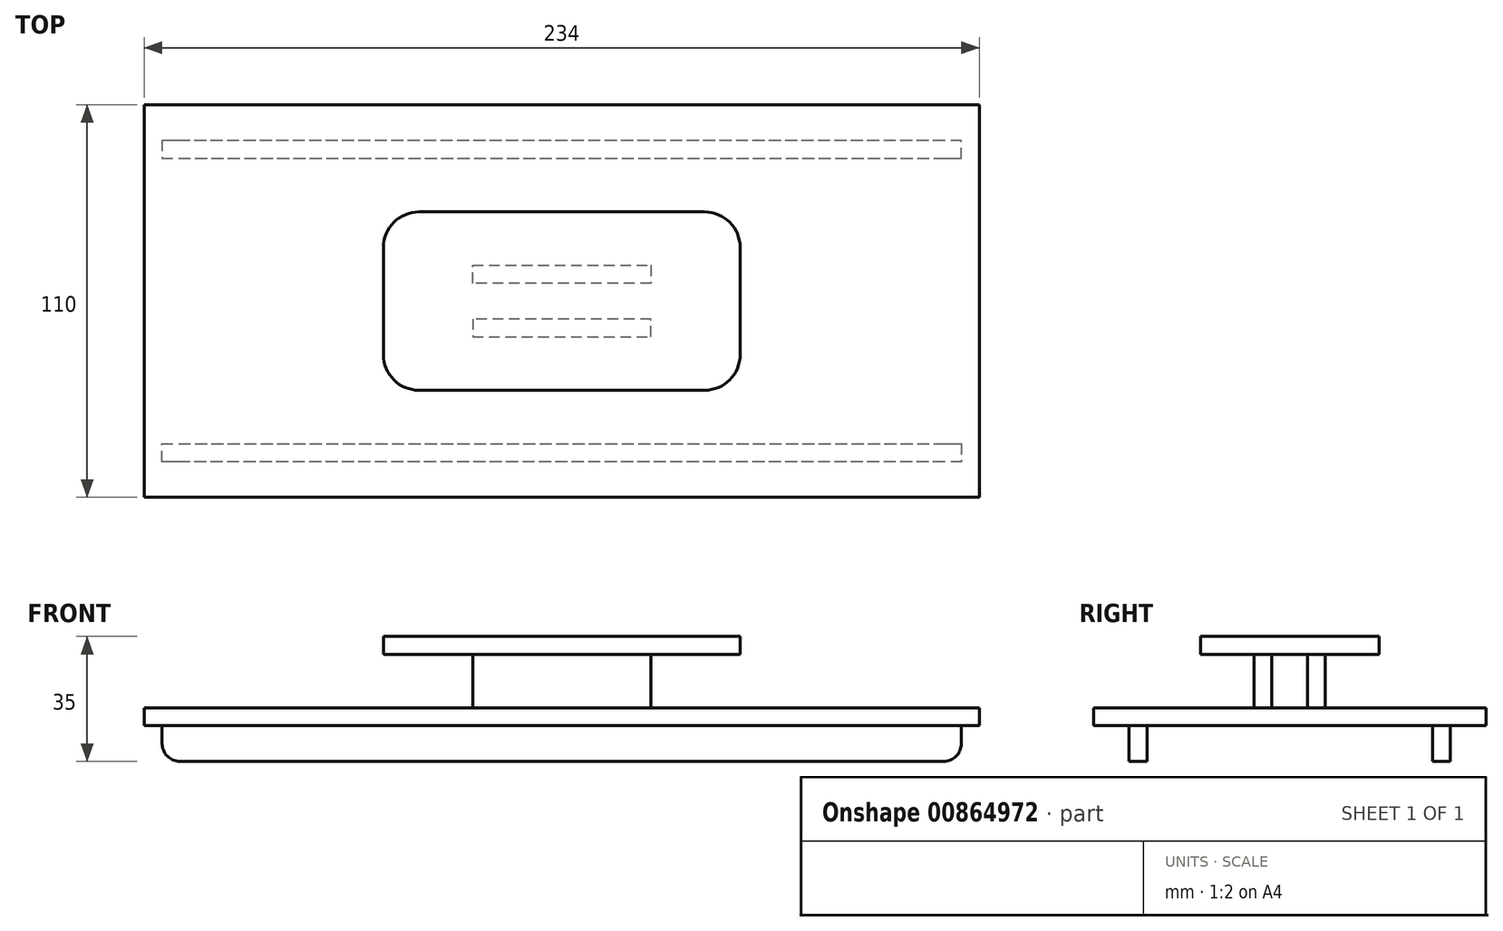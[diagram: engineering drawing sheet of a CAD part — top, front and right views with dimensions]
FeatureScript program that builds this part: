
annotation { "Feature Type Name" : "Feature", "Feature Type Description" : "" }
export const myFeature = defineFeature(function(context is Context, id is Id, definition is map)
    precondition{}
    {
        {
            var Q0;
            Q0=qCreatedBy(makeId("Top.planeOp"),FACE);
            var sketch = newSketch(context, id + "F0", { "sketchPlane" : qUnion([Q0])});
            skLineSegment(sketch, "E0", {"start": v(0, 55) * mm, "end": v(-117, 55) * mm});
            skLineSegment(sketch, "E1", {"start": v(-117, 55) * mm, "end": v(-117, -55) * mm});
            skLineSegment(sketch, "E2", {"start": v(-117, -55) * mm, "end": v(117, -55) * mm});
            skLineSegment(sketch, "E3", {"start": v(117, -55) * mm, "end": v(117, 55) * mm});
            skLineSegment(sketch, "E4", {"start": v(117, 55) * mm, "end": v(0, 55) * mm});
            skSolve(sketch);
        }
        {
            var Q0;
            Q0=makeQuery(id+"F0.imprint","IMPRINT",FACE,{"disambiguationData":[TD([[makeQuery(id+"F0.imprint","IMPRINT",EDGE,{"derivedFrom":sQuery(id+"F0.wireOp",EDGE,"LMLZs7OO-DFld-XzK2-CuK9-4s45sYu2oxnE")}),1.0]])]});
            var Q1;
            Q1=makeQuery(id+"F0.imprint","IMPRINT",FACE,{"disambiguationData":[TD([[makeQuery(id+"F0.imprint","IMPRINT",EDGE,{"derivedFrom":sQuery(id+"F0.wireOp",EDGE,"cvSQRNAl-XPxT-cCQd-Kg4y-DsinOLvF7RYH")}),1.0]])]});
            var Q2;
            Q2=makeQuery(id+"F0.imprint","IMPRINT",FACE,{"disambiguationData":[TD([[makeQuery(id+"F0.imprint","IMPRINT",EDGE,{"derivedFrom":sQuery(id+"F0.wireOp",EDGE,"E0")}),1.0]])]});
            extrude(context, id + "F1", {"entities" : qUnion([Q0, Q1, Q2]), "depth" : 5 * mm, "offsetDistance" : 25 * mm});
        }
        {
            var Q0;
            Q0=qCreatedBy(makeId("Top.planeOp"),FACE);
            var sketch = newSketch(context, id + "F2", { "sketchPlane" : qUnion([Q0])});
            skLineSegment(sketch, "E5", {"start": v(0, 45) * mm, "end": v(-112, 45) * mm});
            skLineSegment(sketch, "E6", {"start": v(-112, 45) * mm, "end": v(-112, 40) * mm});
            skLineSegment(sketch, "E7", {"start": v(-112, 40) * mm, "end": v(112, 40) * mm});
            skLineSegment(sketch, "E8", {"start": v(112, 40) * mm, "end": v(112, 45) * mm});
            skLineSegment(sketch, "E9", {"start": v(112, 45) * mm, "end": v(0, 45) * mm});
            skLineSegment(sketch, "E10.MirrorCS", {"start": v(-112, -45) * mm, "end": v(-112, -40) * mm});
            skLineSegment(sketch, "E11.MirrorCS", {"start": v(112, -40) * mm, "end": v(112, -45) * mm});
            skLineSegment(sketch, "E12.MirrorCS", {"start": v(0, -45) * mm, "end": v(-112, -45) * mm});
            skLineSegment(sketch, "E13.MirrorCS", {"start": v(-112, -40) * mm, "end": v(112, -40) * mm});
            skLineSegment(sketch, "E14.MirrorCS", {"start": v(112, -45) * mm, "end": v(0, -45) * mm});
            skSolve(sketch);
        }
        {
            var Q0;
            Q0=qCreatedBy(makeId("Top.planeOp"),FACE);
            cPlane(context, id + "F3", {"entities" : qUnion([Q0]), "cplaneType" : CPlaneType.OFFSET, "offset" : 25 * mm, "width" : 150 * mm, "height" : 150 * mm});
        }
        {
            var Q0;
            Q0=qCreatedBy(id+"F3.planeOp",FACE);
            var sketch = newSketch(context, id + "F4", { "sketchPlane" : qUnion([Q0])});
            skLineSegment(sketch, "E15", {"start": v(0, 25) * mm, "end": v(-40, 25) * mm});
            skLineSegment(sketch, "E16", {"start": v(-50, 15) * mm, "end": v(-50, -15) * mm});
            skLineSegment(sketch, "E17", {"start": v(-40, -25) * mm, "end": v(40, -25) * mm});
            skLineSegment(sketch, "E18", {"start": v(50, -15) * mm, "end": v(50, 15) * mm});
            skLineSegment(sketch, "E19", {"start": v(40, 25) * mm, "end": v(0, 25) * mm});
            skPoint(sketch, "E20.visualSharp", {"position": v(-50, 25) * mm});
            skArc(sketch, "E20.filletArc", {"start": v(-40, 25) * mm, "mid": v(-47.07, 22.07) * mm, "end": v(-50, 15) * mm});
            skPoint(sketch, "E21.visualSharp", {"position": v(50, 25) * mm});
            skArc(sketch, "E21.filletArc", {"start": v(50, 15) * mm, "mid": v(47.07, 22.07) * mm, "end": v(40, 25) * mm});
            skPoint(sketch, "E22.visualSharp", {"position": v(50, -25) * mm});
            skArc(sketch, "E22.filletArc", {"start": v(40, -25) * mm, "mid": v(47.07, -22.07) * mm, "end": v(50, -15) * mm});
            skPoint(sketch, "E23.visualSharp", {"position": v(-50, -25) * mm});
            skArc(sketch, "E23.filletArc", {"start": v(-50, -15) * mm, "mid": v(-47.07, -22.07) * mm, "end": v(-40, -25) * mm});
            skSolve(sketch);
        }
        {
            var Q0;
            Q0=qCreatedBy(makeId("Top.planeOp"),FACE);
            cPlane(context, id + "F5", {"entities" : qUnion([Q0]), "cplaneType" : CPlaneType.OFFSET, "offset" : 5 * mm, "width" : 150 * mm, "height" : 150 * mm});
        }
        {
            var Q0;
            Q0=qCreatedBy(id+"F5.planeOp",FACE);
            var sketch = newSketch(context, id + "F6", { "sketchPlane" : qUnion([Q0])});
            skLineSegment(sketch, "E24", {"start": v(0, 5) * mm, "end": v(-25, 5) * mm});
            skLineSegment(sketch, "E25", {"start": v(-25, 5) * mm, "end": v(-25, 10) * mm});
            skLineSegment(sketch, "E26", {"start": v(-25, 10) * mm, "end": v(25, 10) * mm});
            skLineSegment(sketch, "E27", {"start": v(25, 10) * mm, "end": v(25, 5) * mm});
            skLineSegment(sketch, "E28", {"start": v(25, 5) * mm, "end": v(0, 5) * mm});
            skLineSegment(sketch, "E29.MirrorCS", {"start": v(25, -5) * mm, "end": v(0, -5) * mm});
            skLineSegment(sketch, "E30.MirrorCS", {"start": v(-25, -10) * mm, "end": v(25, -10) * mm});
            skLineSegment(sketch, "E31.MirrorCS", {"start": v(25, -10) * mm, "end": v(25, -5) * mm});
            skLineSegment(sketch, "E32.MirrorCS", {"start": v(0, -5) * mm, "end": v(-25, -5) * mm});
            skLineSegment(sketch, "E33.MirrorCS", {"start": v(-25, -5) * mm, "end": v(-25, -10) * mm});
            skSolve(sketch);
        }
        {
            var Q0;
            Q0=makeQuery(id+"F2.imprint","IMPRINT",FACE,{"disambiguationData":[TD([[makeQuery(id+"F2.imprint","IMPRINT",EDGE,{"derivedFrom":sQuery(id+"F2.wireOp",EDGE,"E10.MirrorCS")}),-1.0]])]});
            var Q1;
            Q1=makeQuery(id+"F2.imprint","IMPRINT",FACE,{"disambiguationData":[TD([[makeQuery(id+"F2.imprint","IMPRINT",EDGE,{"derivedFrom":sQuery(id+"F2.wireOp",EDGE,"E5")}),1.0]])]});
            extrude(context, id + "F7", {"entities" : qUnion([Q0, Q1]), "oppositeDirection" : true, "depth" : 10 * mm, "offsetDistance" : 25 * mm});
        }
        {
            var Q0;
            Q0=makeQuery(id+"F7.opExtrude","CAP_EDGE",EDGE,{"disambiguationData":[OSD([sQuery(id+"F2.wireOp",EDGE,"E10.MirrorCS")])],"isStart":false});
            var Q1;
            Q1=makeQuery(id+"F7.opExtrude","CAP_EDGE",EDGE,{"disambiguationData":[OSD([sQuery(id+"F2.wireOp",EDGE,"E11.MirrorCS")])],"isStart":false});
            var Q2;
            Q2=makeQuery(id+"F7.opExtrude","CAP_EDGE",EDGE,{"disambiguationData":[OSD([sQuery(id+"F2.wireOp",EDGE,"E8")])],"isStart":false});
            var Q3;
            Q3=makeQuery(id+"F7.opExtrude","CAP_EDGE",EDGE,{"disambiguationData":[OSD([sQuery(id+"F2.wireOp",EDGE,"E6")])],"isStart":false});
            fillet(context, id + "F8", {"entities" : qUnion([Q0, Q1, Q2, Q3]), "radius" : 5 * mm, "tangentPropagation" : true, "allowEdgeOverflow" : false});
        }
        {
            var Q0;
            Q0=makeQuery(id+"F6.imprint","IMPRINT",FACE,{"disambiguationData":[TD([[makeQuery(id+"F6.imprint","IMPRINT",EDGE,{"derivedFrom":sQuery(id+"F6.wireOp",EDGE,"E29.MirrorCS")}),1.0]])]});
            var Q1;
            Q1=makeQuery(id+"F6.imprint","IMPRINT",FACE,{"disambiguationData":[TD([[makeQuery(id+"F6.imprint","IMPRINT",EDGE,{"derivedFrom":sQuery(id+"F6.wireOp",EDGE,"E24")}),-1.0]])]});
            extrude(context, id + "F9", {"entities" : qUnion([Q0, Q1]), "depth" : 15 * mm, "offsetDistance" : 25 * mm});
        }
        {
            var Q0;
            Q0=makeQuery(id+"F4.imprint","IMPRINT",FACE,{"disambiguationData":[TD([[makeQuery(id+"F4.imprint","IMPRINT",EDGE,{"derivedFrom":sQuery(id+"F4.wireOp",EDGE,"E15")}),1.0]])]});
            extrude(context, id + "F10", {"entities" : qUnion([Q0]), "oppositeDirection" : true, "depth" : 5 * mm, "offsetDistance" : 25 * mm});
        }
    });
